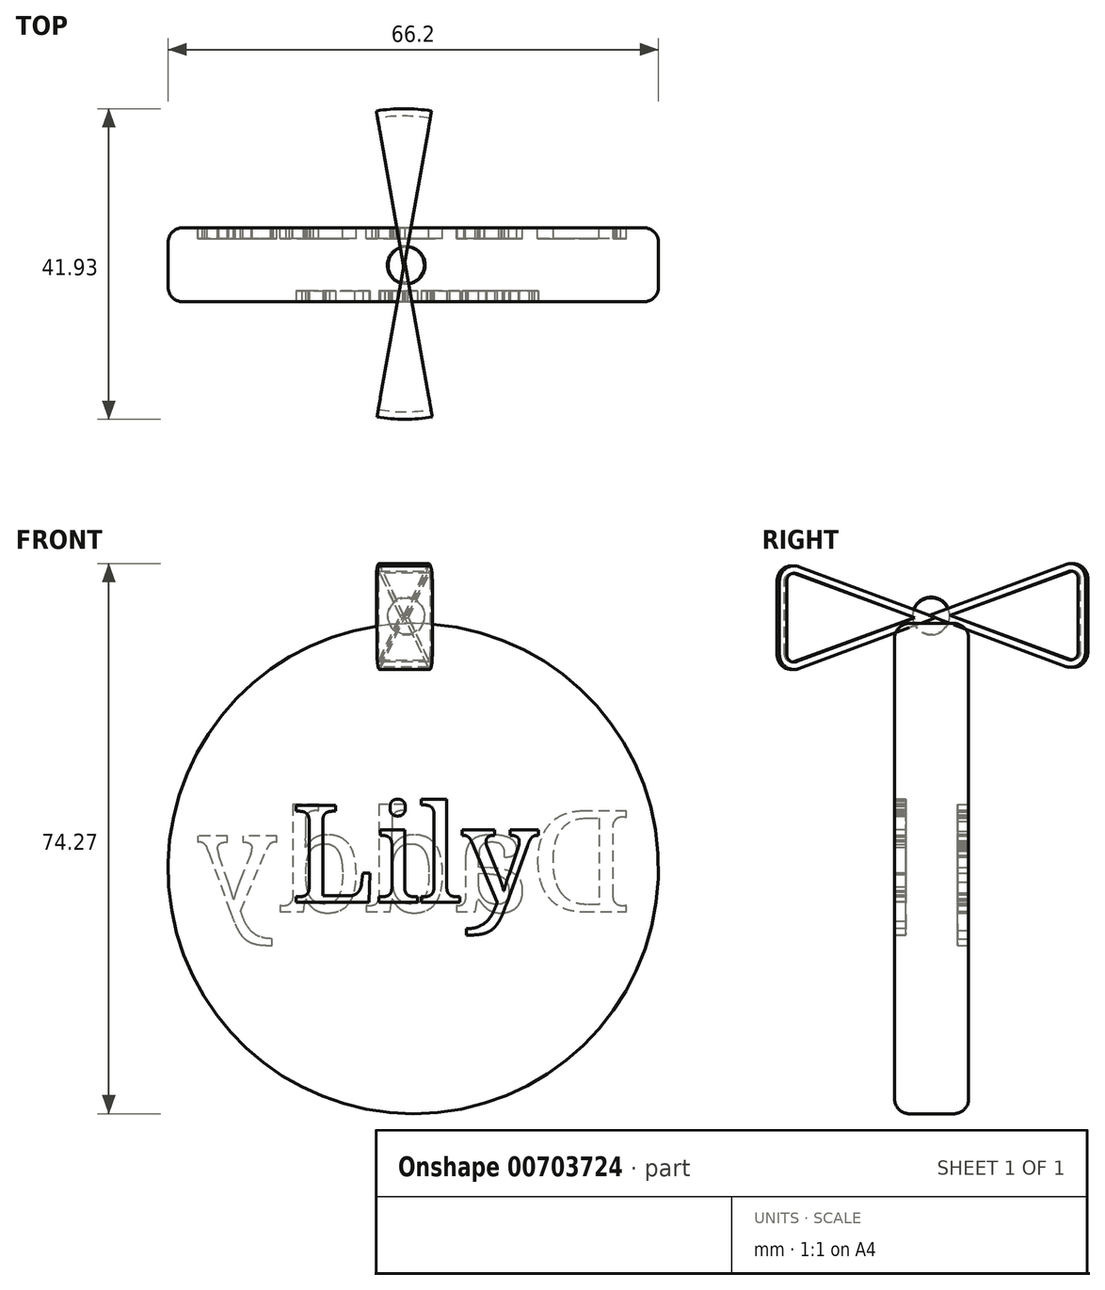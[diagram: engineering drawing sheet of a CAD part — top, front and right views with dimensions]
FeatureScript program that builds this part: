
annotation { "Feature Type Name" : "Feature", "Feature Type Description" : "" }
export const myFeature = defineFeature(function(context is Context, id is Id, definition is map)
    precondition{}
    {
        {
            var Q0;
            Q0=qCreatedBy(makeId("Top.planeOp"),FACE);
            var sketch = newSketch(context, id + "F0", { "sketchPlane" : qUnion([Q0])});
            skCircle(sketch, "E0", {"center": v(-32.52, -14.07) * mm, "radius": 2.53 * mm});
            skSolve(sketch);
        }
        {
            var Q0;
            Q0=sQuery(id+"F0.wireOp",EDGE,"E0");
            extrude(context, id + "F1", {"bodyType" : ToolBodyType.SURFACE, "surfaceEntities" : qUnion([Q0]), "depth" : 64.1 * mm, "offsetDistance" : 25 * mm});
        }
        {
            var Q0;
            Q0=qCreatedBy(makeId("Front.planeOp"),FACE);
            var sketch = newSketch(context, id + "F2", { "sketchPlane" : qUnion([Q0])});
            skCircle(sketch, "E1", {"center": v(-33.44, 81.3) * mm, "radius": 33.1 * mm});
            skSolve(sketch);
        }
        {
            var Q0;
            Q0=makeQuery(id+"F2.imprint","IMPRINT",FACE,{"disambiguationData":[TD([[makeQuery(id+"F2.imprint","IMPRINT",EDGE,{"derivedFrom":sQuery(id+"F2.wireOp",EDGE,"E1")}),1.0]])]});
            extrude(context, id + "F3", {"entities" : qUnion([Q0]), "depth" : 10 * mm, "offsetDistance" : 25 * mm});
        }
        {
            var Q0;
            Q0=makeQuery(id+"F3.opExtrude","SWEPT_BODY",BODY,{"disambiguationData":[OSD([sQuery(id+"F2.wireOp",EDGE,"E1")])]});
            transform(context, id + "F4", {"entities" : qUnion([Q0]), "transformType" : TransformType.TRANSLATION_3D, "dx" : 0.8 * mm, "dy" : -9.2 * mm, "dz" : 0 * mm, "makeCopy" : false});
        }
        {
            var Q0;
            Q0=makeQuery(id+"F3.opExtrude","CAP_EDGE",EDGE,{"disambiguationData":[OSD([sQuery(id+"F2.wireOp",EDGE,"E1")])],"isStart":false});
            var Q1;
            Q1=makeQuery(id+"F3.opExtrude","CAP_EDGE",EDGE,{"disambiguationData":[OSD([sQuery(id+"F2.wireOp",EDGE,"E1")])],"isStart":true});
            fillet(context, id + "F5", {"entities" : qUnion([Q0, Q1]), "radius" : 2 * mm, "tangentPropagation" : true, "allowEdgeOverflow" : false});
        }
        {
            var Q0;
            Q0=makeQuery(id+"F3.opExtrude","CAP_FACE",FACE,{"disambiguationData":[OSD([sQuery(id+"F2.wireOp",EDGE,"E1")])],"isStart":false});
            var sketch = newSketch(context, id + "F6", { "sketchPlane" : qUnion([Q0])});
            skText(sketch, "E2", { "text": "Lily", "fontName": "NotoSerif-Regular.ttf"});
            const initialGuessF6  = {"E2": [-0.04913, 0.07672, 1, 0, 0.01321]};
            skSetInitialGuess(sketch, initialGuessF6);
            skSolve(sketch);
        }
        {
            var Q0;
            Q0=makeQuery(id+"F6.imprint","IMPRINT",FACE,{"disambiguationData":[TD([[makeQuery(id+"F6.imprint","IMPRINT",EDGE,{"derivedFrom":sQuery(id+"F6.wireOp",EDGE,"E2.sketch_text.stroke-0")}),-1.0]])]});
            var Q1;
            Q1=makeQuery(id+"F6.imprint","IMPRINT",FACE,{"disambiguationData":[TD([[makeQuery(id+"F6.imprint","IMPRINT",EDGE,{"derivedFrom":sQuery(id+"F6.wireOp",EDGE,"E2.sketch_text.stroke-30")}),-1.0]])]});
            var Q2;
            Q2=makeQuery(id+"F6.imprint","IMPRINT",FACE,{"disambiguationData":[TD([[makeQuery(id+"F6.imprint","IMPRINT",EDGE,{"derivedFrom":sQuery(id+"F6.wireOp",EDGE,"E2.sketch_text.stroke-52")}),-1.0]])]});
            var Q3;
            Q3=makeQuery(id+"F6.imprint","IMPRINT",FACE,{"disambiguationData":[TD([[makeQuery(id+"F6.imprint","IMPRINT",EDGE,{"derivedFrom":sQuery(id+"F6.wireOp",EDGE,"E2.sketch_text.stroke-68")}),-1.0]])]});
            var Q4;
            Q4=makeQuery(id+"F6.imprint","IMPRINT",FACE,{"disambiguationData":[TD([[makeQuery(id+"F6.imprint","IMPRINT",EDGE,{"derivedFrom":sQuery(id+"F6.wireOp",EDGE,"E2.sketch_text.stroke-90")}),-1.0]])]});
            extrude(context, id + "F7", {"entities" : qUnion([Q0, Q1, Q2, Q3, Q4]), "operationType" : NewBodyOperationType.REMOVE, "oppositeDirection" : true, "depth" : 1.5 * mm, "offsetDistance" : 25 * mm});
        }
        {
            var Q0;
            Q0=makeQuery(id+"F3.opExtrude","CAP_FACE",FACE,{"disambiguationData":[OSD([sQuery(id+"F2.wireOp",EDGE,"E1")])],"isStart":true});
            var sketch = newSketch(context, id + "F8", { "sketchPlane" : qUnion([Q0])});
            skText(sketch, "E3", { "text": "Daddy", "fontName": "NotoSerif-Regular.ttf"});
            const initialGuessF8  = {"E3": [0.00313, 0.07549, 1, 0, 0.01368]};
            skSetInitialGuess(sketch, initialGuessF8);
            skSolve(sketch);
        }
        {
            var Q0;
            Q0=makeQuery(id+"F8.imprint","IMPRINT",FACE,{"disambiguationData":[TD([[makeQuery(id+"F8.imprint","IMPRINT",EDGE,{"derivedFrom":sQuery(id+"F8.wireOp",EDGE,"E3.sketch_text.stroke-84")}),-1.0]])]});
            var Q1;
            Q1=makeQuery(id+"F8.imprint","IMPRINT",FACE,{"disambiguationData":[TD([[makeQuery(id+"F8.imprint","IMPRINT",EDGE,{"derivedFrom":sQuery(id+"F8.wireOp",EDGE,"E3.sketch_text.stroke-32")}),-1.0]])]});
            var Q2;
            Q2=makeQuery(id+"F8.imprint","IMPRINT",FACE,{"disambiguationData":[TD([[makeQuery(id+"F8.imprint","IMPRINT",EDGE,{"derivedFrom":sQuery(id+"F8.wireOp",EDGE,"E3.sketch_text.stroke-0")}),-1.0]])]});
            var Q3;
            Q3=makeQuery(id+"F8.imprint","IMPRINT",FACE,{"disambiguationData":[TD([[makeQuery(id+"F8.imprint","IMPRINT",EDGE,{"derivedFrom":sQuery(id+"F8.wireOp",EDGE,"E3.sketch_text.stroke-136")}),-1.0]])]});
            var Q4;
            Q4=makeQuery(id+"F8.imprint","IMPRINT",FACE,{"disambiguationData":[TD([[makeQuery(id+"F8.imprint","IMPRINT",EDGE,{"derivedFrom":sQuery(id+"F8.wireOp",EDGE,"E3.sketch_text.stroke-188")}),-1.0]])]});
            extrude(context, id + "F9", {"entities" : qUnion([Q0, Q1, Q2, Q3, Q4]), "operationType" : NewBodyOperationType.REMOVE, "oppositeDirection" : true, "depth" : 1.5 * mm, "offsetDistance" : 25 * mm});
        }
        {
            var Q0;
            Q0=qCreatedBy(makeId("Top.planeOp"),FACE);
            var sketch = newSketch(context, id + "F10", { "sketchPlane" : qUnion([Q0])});
            skLineSegment(sketch, "E4", {"start": v(27.8, 25.64) * mm, "end": v(27.8, 20.64) * mm});
            skArc(sketch, "E5", {"start": v(27.8, 20.64) * mm, "mid": v(30.36, 23.14) * mm, "end": v(27.8, 25.64) * mm});
            skSolve(sketch);
        }
        {
            var Q0;
            Q0=makeQuery(id+"F10.imprint","IMPRINT",FACE,{"disambiguationData":[TD([[makeQuery(id+"F10.imprint","IMPRINT",EDGE,{"derivedFrom":sQuery(id+"F10.wireOp",EDGE,"E4")}),1.0]])]});
            var Q1;
            Q1=sQuery(id+"F10.wireOp",EDGE,"E4");
            revolve(context, id + "F11", {"surfaceOperationType" : NewSurfaceOperationType.NEW, "entities" : qUnion([Q0]), "axis" : qUnion([Q1]), "revolveType" : RevolveType.FULL});
        }
        {
            var Q0;
            Q0=qCreatedBy(makeId("Right.planeOp"),FACE);
            var sketch = newSketch(context, id + "F12", { "sketchPlane" : qUnion([Q0])});
            skLineSegment(sketch, "E6", {"start": v(26.62, -22.13) * mm, "end": v(45.4, -15.25) * mm});
            skLineSegment(sketch, "E7", {"start": v(48.08, -17.13) * mm, "end": v(48.08, -27.13) * mm});
            skLineSegment(sketch, "E8", {"start": v(45.4, -29) * mm, "end": v(26.62, -22.13) * mm});
            skPoint(sketch, "E9.visualSharp", {"position": v(48.08, -14.26) * mm});
            skArc(sketch, "E9.filletArc", {"start": v(48.08, -17.13) * mm, "mid": v(47.23, -15.49) * mm, "end": v(45.4, -15.25) * mm});
            skPoint(sketch, "E10.visualSharp", {"position": v(48.08, -29.99) * mm});
            skArc(sketch, "E10.filletArc", {"start": v(45.4, -29) * mm, "mid": v(47.23, -28.77) * mm, "end": v(48.08, -27.13) * mm});
            skLineSegment(sketch, "E11", {"start": v(26.62, -17.75) * mm, "end": v(26.62, -25.58) * mm});
            skLineSegment(sketch, "E12.0", {"start": v(29.52, -22.13) * mm, "end": v(45.74, -16.19) * mm});
            skLineSegment(sketch, "E12.1", {"start": v(45.74, -28.07) * mm, "end": v(29.52, -22.13) * mm});
            skArc(sketch, "E12.2", {"start": v(47.08, -17.13) * mm, "mid": v(46.66, -16.3) * mm, "end": v(45.74, -16.19) * mm});
            skLineSegment(sketch, "E12.3", {"start": v(47.08, -17.13) * mm, "end": v(47.08, -27.13) * mm});
            skArc(sketch, "E12.4", {"start": v(45.74, -28.07) * mm, "mid": v(46.66, -27.95) * mm, "end": v(47.08, -27.13) * mm});
            skSolve(sketch);
        }
        {
            var Q0;
            Q0=makeQuery(id+"F12.imprint","IMPRINT",FACE,{"disambiguationData":[TD([[makeQuery(id+"F12.imprint","IMPRINT",EDGE,{"derivedFrom":sQuery(id+"F12.wireOp",EDGE,"E7")}),-1.0]])]});
            var Q1;
            Q1=sQuery(id+"F12.wireOp",EDGE,"E11");
            revolve(context, id + "F13", {"surfaceOperationType" : NewSurfaceOperationType.NEW, "entities" : qUnion([Q0]), "axis" : qUnion([Q1]), "revolveType" : RevolveType.SYMMETRIC, "angle" : 20 * degree});
        }
        {
            var Q0;
            Q0=makeQuery(id+"F13.opRevolve","SWEPT_BODY",BODY,{"disambiguationData":[OSD([sQuery(id+"F12.wireOp",EDGE,"E6"),sQuery(id+"F12.wireOp",EDGE,"E7"),sQuery(id+"F12.wireOp",EDGE,"E8"),sQuery(id+"F12.wireOp",EDGE,"E9.filletArc"),sQuery(id+"F12.wireOp",EDGE,"E10.filletArc"),sQuery(id+"F12.wireOp",EDGE,"E11"),sQuery(id+"F12.wireOp",EDGE,"E12.0"),sQuery(id+"F12.wireOp",EDGE,"E12.1"),sQuery(id+"F12.wireOp",EDGE,"E12.2"),sQuery(id+"F12.wireOp",EDGE,"E12.3"),sQuery(id+"F12.wireOp",EDGE,"E12.4")])]});
            transform(context, id + "F14", {"entities" : qUnion([Q0]), "transformType" : TransformType.TRANSLATION_3D, "dx" : 27.5 * mm, "dy" : -3.8 * mm, "dz" : 22.2 * mm, "makeCopy" : false});
        }
        {
            var Q0;
            Q0=makeQuery(id+"F13.opRevolve","SWEPT_BODY",BODY,{"disambiguationData":[OSD([sQuery(id+"F12.wireOp",EDGE,"E6"),sQuery(id+"F12.wireOp",EDGE,"E7"),sQuery(id+"F12.wireOp",EDGE,"E8"),sQuery(id+"F12.wireOp",EDGE,"E9.filletArc"),sQuery(id+"F12.wireOp",EDGE,"E10.filletArc"),sQuery(id+"F12.wireOp",EDGE,"E11"),sQuery(id+"F12.wireOp",EDGE,"E12.0"),sQuery(id+"F12.wireOp",EDGE,"E12.1"),sQuery(id+"F12.wireOp",EDGE,"E12.2"),sQuery(id+"F12.wireOp",EDGE,"E12.3"),sQuery(id+"F12.wireOp",EDGE,"E12.4")])]});
            transform(context, id + "F15", {"entities" : qUnion([Q0]), "transformType" : TransformType.TRANSLATION_3D, "dx" : 47.3 * mm, "dy" : 0 * mm, "dz" : -32.4 * mm, "makeCopy" : true});
        }
        {
            var Q0;
            Q0=makeQuery(id+"F15.opPattern","COPY",BODY,{"derivedFrom":makeQuery(id+"F13.opRevolve","SWEPT_BODY",BODY,{"disambiguationData":[OSD([sQuery(id+"F12.wireOp",EDGE,"E6"),sQuery(id+"F12.wireOp",EDGE,"E7"),sQuery(id+"F12.wireOp",EDGE,"E8"),sQuery(id+"F12.wireOp",EDGE,"E9.filletArc"),sQuery(id+"F12.wireOp",EDGE,"E10.filletArc"),sQuery(id+"F12.wireOp",EDGE,"E11"),sQuery(id+"F12.wireOp",EDGE,"E12.0"),sQuery(id+"F12.wireOp",EDGE,"E12.1"),sQuery(id+"F12.wireOp",EDGE,"E12.2"),sQuery(id+"F12.wireOp",EDGE,"E12.3"),sQuery(id+"F12.wireOp",EDGE,"E12.4")])]}),"instanceName":"1"});
            var Q1;
            Q1=makeQuery(id+"F15.opPattern","COPY",FACE,{"derivedFrom":makeQuery(id+"F13.opRevolve","SWEPT_FACE",FACE,{"disambiguationData":[OSD([sQuery(id+"F12.wireOp",EDGE,"E7")])]}),"instanceName":"1"});
            transform(context, id + "F16", {"entities" : qUnion([Q0]), "transformType" : TransformType.ROTATION, "transformAxis" : qUnion([Q1]), "angle" : 180 * degree, "oppositeDirection" : true, "makeCopy" : false});
        }
        {
            var Q0;
            Q0=makeQuery(id+"F15.opPattern","COPY",BODY,{"derivedFrom":makeQuery(id+"F13.opRevolve","SWEPT_BODY",BODY,{"disambiguationData":[OSD([sQuery(id+"F12.wireOp",EDGE,"E6"),sQuery(id+"F12.wireOp",EDGE,"E7"),sQuery(id+"F12.wireOp",EDGE,"E8"),sQuery(id+"F12.wireOp",EDGE,"E9.filletArc"),sQuery(id+"F12.wireOp",EDGE,"E10.filletArc"),sQuery(id+"F12.wireOp",EDGE,"E11"),sQuery(id+"F12.wireOp",EDGE,"E12.0"),sQuery(id+"F12.wireOp",EDGE,"E12.1"),sQuery(id+"F12.wireOp",EDGE,"E12.2"),sQuery(id+"F12.wireOp",EDGE,"E12.3"),sQuery(id+"F12.wireOp",EDGE,"E12.4")])]}),"instanceName":"1"});
            transform(context, id + "F17", {"entities" : qUnion([Q0]), "transformType" : TransformType.TRANSLATION_3D, "dx" : -47.2 * mm, "dy" : 1 * mm, "dz" : 32.1 * mm, "makeCopy" : false});
        }
        {
            var Q0;
            Q0=makeQuery(id+"F11.opRevolve","SWEPT_BODY",BODY,{"disambiguationData":[OSD([sQuery(id+"F10.wireOp",EDGE,"E4"),sQuery(id+"F10.wireOp",EDGE,"E5")])]});
            var Q1;
            Q1=makeQuery(id+"F13.opRevolve","SWEPT_BODY",BODY,{"disambiguationData":[OSD([sQuery(id+"F12.wireOp",EDGE,"E6"),sQuery(id+"F12.wireOp",EDGE,"E7"),sQuery(id+"F12.wireOp",EDGE,"E8"),sQuery(id+"F12.wireOp",EDGE,"E9.filletArc"),sQuery(id+"F12.wireOp",EDGE,"E10.filletArc"),sQuery(id+"F12.wireOp",EDGE,"E11"),sQuery(id+"F12.wireOp",EDGE,"E12.0"),sQuery(id+"F12.wireOp",EDGE,"E12.1"),sQuery(id+"F12.wireOp",EDGE,"E12.2"),sQuery(id+"F12.wireOp",EDGE,"E12.3"),sQuery(id+"F12.wireOp",EDGE,"E12.4")])]});
            var Q2;
            Q2=makeQuery(id+"F15.opPattern","COPY",BODY,{"derivedFrom":makeQuery(id+"F13.opRevolve","SWEPT_BODY",BODY,{"disambiguationData":[OSD([sQuery(id+"F12.wireOp",EDGE,"E6"),sQuery(id+"F12.wireOp",EDGE,"E7"),sQuery(id+"F12.wireOp",EDGE,"E8"),sQuery(id+"F12.wireOp",EDGE,"E9.filletArc"),sQuery(id+"F12.wireOp",EDGE,"E10.filletArc"),sQuery(id+"F12.wireOp",EDGE,"E11"),sQuery(id+"F12.wireOp",EDGE,"E12.0"),sQuery(id+"F12.wireOp",EDGE,"E12.1"),sQuery(id+"F12.wireOp",EDGE,"E12.2"),sQuery(id+"F12.wireOp",EDGE,"E12.3"),sQuery(id+"F12.wireOp",EDGE,"E12.4")])]}),"instanceName":"1"});
            transform(context, id + "F18", {"entities" : qUnion([Q0, Q1, Q2]), "transformType" : TransformType.TRANSLATION_3D, "dx" : -61.4 * mm, "dy" : -37.4 * mm, "dz" : 116.5 * mm, "makeCopy" : false});
        }
        {
            var Q0;
            Q0=makeQuery(id+"F11.opRevolve","SWEPT_BODY",BODY,{"disambiguationData":[OSD([sQuery(id+"F10.wireOp",EDGE,"E4"),sQuery(id+"F10.wireOp",EDGE,"E5")])]});
            var Q1;
            Q1=makeQuery(id+"F13.opRevolve","SWEPT_BODY",BODY,{"disambiguationData":[OSD([sQuery(id+"F12.wireOp",EDGE,"E6"),sQuery(id+"F12.wireOp",EDGE,"E7"),sQuery(id+"F12.wireOp",EDGE,"E8"),sQuery(id+"F12.wireOp",EDGE,"E9.filletArc"),sQuery(id+"F12.wireOp",EDGE,"E10.filletArc"),sQuery(id+"F12.wireOp",EDGE,"E11"),sQuery(id+"F12.wireOp",EDGE,"E12.0"),sQuery(id+"F12.wireOp",EDGE,"E12.1"),sQuery(id+"F12.wireOp",EDGE,"E12.2"),sQuery(id+"F12.wireOp",EDGE,"E12.3"),sQuery(id+"F12.wireOp",EDGE,"E12.4")])]});
            var Q2;
            Q2=makeQuery(id+"F15.opPattern","COPY",BODY,{"derivedFrom":makeQuery(id+"F13.opRevolve","SWEPT_BODY",BODY,{"disambiguationData":[OSD([sQuery(id+"F12.wireOp",EDGE,"E6"),sQuery(id+"F12.wireOp",EDGE,"E7"),sQuery(id+"F12.wireOp",EDGE,"E8"),sQuery(id+"F12.wireOp",EDGE,"E9.filletArc"),sQuery(id+"F12.wireOp",EDGE,"E10.filletArc"),sQuery(id+"F12.wireOp",EDGE,"E11"),sQuery(id+"F12.wireOp",EDGE,"E12.0"),sQuery(id+"F12.wireOp",EDGE,"E12.1"),sQuery(id+"F12.wireOp",EDGE,"E12.2"),sQuery(id+"F12.wireOp",EDGE,"E12.3"),sQuery(id+"F12.wireOp",EDGE,"E12.4")])]}),"instanceName":"1"});
            transform(context, id + "F19", {"entities" : qUnion([Q0, Q1, Q2]), "transformType" : TransformType.TRANSLATION_3D, "dx" : 0 * mm, "dy" : 0 * mm, "dz" : -1.1 * mm, "makeCopy" : false});
        }
    });
